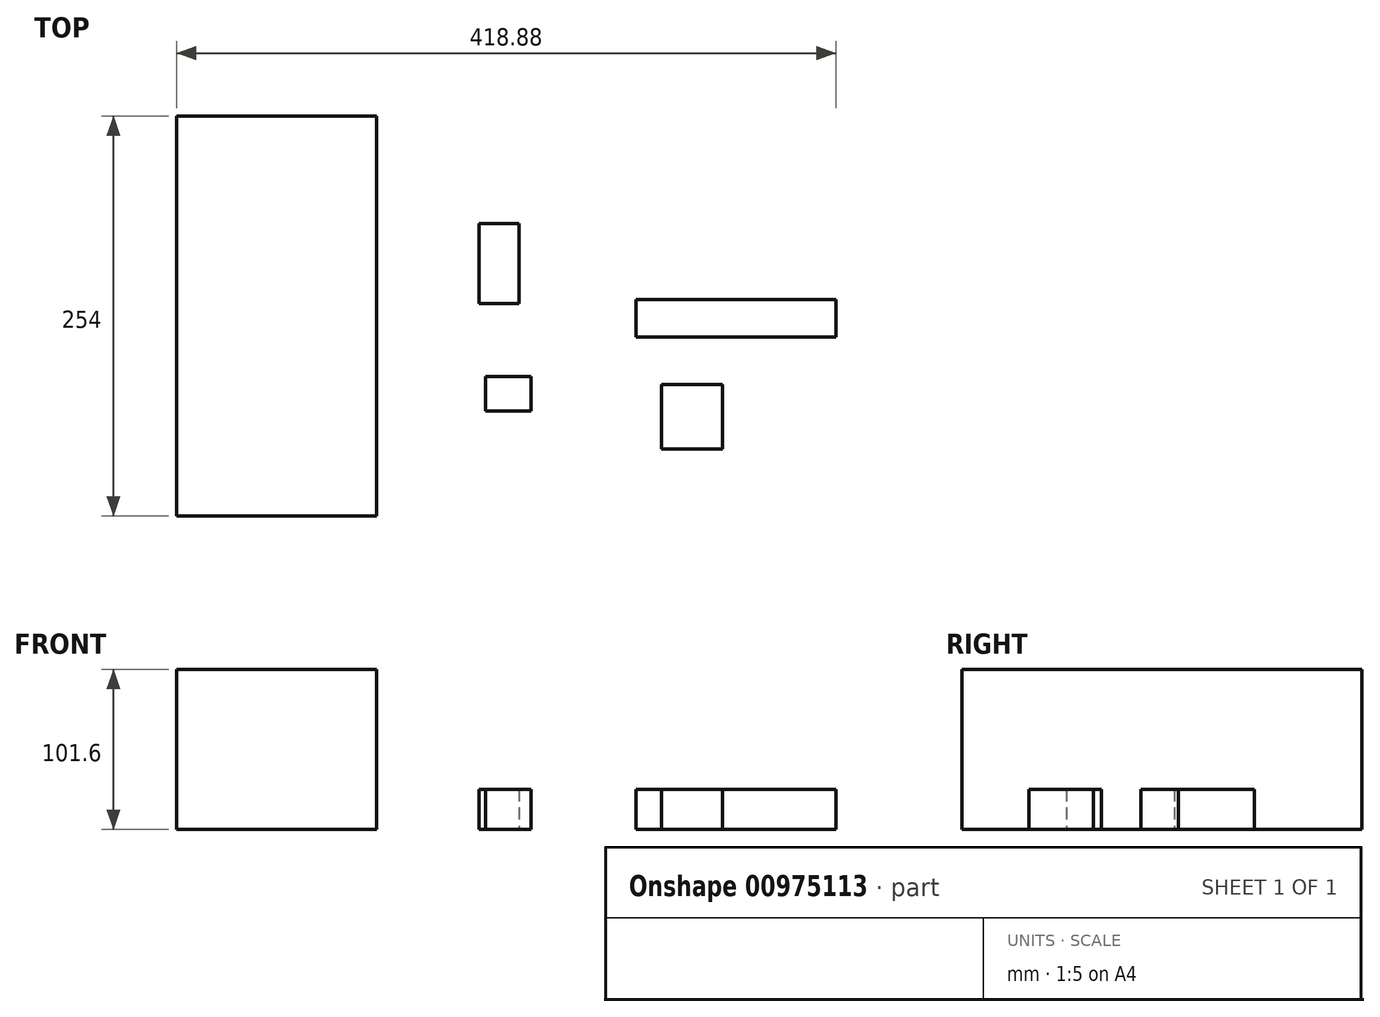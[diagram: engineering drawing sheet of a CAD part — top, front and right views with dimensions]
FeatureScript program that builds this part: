
annotation { "Feature Type Name" : "Feature", "Feature Type Description" : "" }
export const myFeature = defineFeature(function(context is Context, id is Id, definition is map)
    precondition{}
    {
        {
            var Q0;
            Q0=qCreatedBy(makeId("Top.planeOp"),FACE);
            var sketch = newSketch(context, id + "F0", { "sketchPlane" : qUnion([Q0])});
            skLineSegment(sketch, "E0.bottom", {"start": v(-93.4, 74.62) * mm, "end": v(-68, 74.62) * mm});
            skLineSegment(sketch, "E0.top", {"start": v(-93.4, 23.82) * mm, "end": v(-68, 23.82) * mm});
            skLineSegment(sketch, "E0.left", {"start": v(-93.4, 74.62) * mm, "end": v(-93.4, 23.82) * mm});
            skLineSegment(sketch, "E0.right", {"start": v(-68, 74.62) * mm, "end": v(-68, 23.82) * mm});
            skLineSegment(sketch, "E1.bottom", {"start": v(6.4, 26.18) * mm, "end": v(133.4, 26.18) * mm});
            skLineSegment(sketch, "E1.top", {"start": v(6.4, 2.56) * mm, "end": v(133.4, 2.56) * mm});
            skLineSegment(sketch, "E1.left", {"start": v(6.4, 26.18) * mm, "end": v(6.4, 2.56) * mm});
            skLineSegment(sketch, "E1.right", {"start": v(133.4, 26.18) * mm, "end": v(133.4, 2.56) * mm});
            skLineSegment(sketch, "E2.bottom", {"start": v(22.73, -27.56) * mm, "end": v(61.5, -27.56) * mm});
            skLineSegment(sketch, "E2.top", {"start": v(22.73, -68.7) * mm, "end": v(61.5, -68.7) * mm});
            skLineSegment(sketch, "E2.left", {"start": v(22.73, -27.56) * mm, "end": v(22.73, -68.7) * mm});
            skLineSegment(sketch, "E2.right", {"start": v(61.5, -27.56) * mm, "end": v(61.5, -68.7) * mm});
            skLineSegment(sketch, "E3.bottom", {"start": v(-89.06, -22.64) * mm, "end": v(-60.33, -22.64) * mm});
            skLineSegment(sketch, "E3.top", {"start": v(-89.06, -44.68) * mm, "end": v(-60.33, -44.68) * mm});
            skLineSegment(sketch, "E3.left", {"start": v(-89.06, -22.64) * mm, "end": v(-89.06, -44.68) * mm});
            skLineSegment(sketch, "E3.right", {"start": v(-60.33, -22.64) * mm, "end": v(-60.33, -44.68) * mm});
            skSolve(sketch);
        }
        {
            var Q0;
            Q0=makeQuery(id+"F0.imprint","IMPRINT",FACE,{"disambiguationData":[TD([[makeQuery(id+"F0.imprint","IMPRINT",EDGE,{"derivedFrom":sQuery(id+"F0.wireOp",EDGE,"E0.bottom")}),-1.0]])]});
            var Q1;
            Q1=makeQuery(id+"F0.imprint","IMPRINT",FACE,{"disambiguationData":[TD([[makeQuery(id+"F0.imprint","IMPRINT",EDGE,{"derivedFrom":sQuery(id+"F0.wireOp",EDGE,"E1.bottom")}),-1.0]])]});
            var Q2;
            Q2=makeQuery(id+"F0.imprint","IMPRINT",FACE,{"disambiguationData":[TD([[makeQuery(id+"F0.imprint","IMPRINT",EDGE,{"derivedFrom":sQuery(id+"F0.wireOp",EDGE,"E2.bottom")}),-1.0]])]});
            var Q3;
            Q3=makeQuery(id+"F0.imprint","IMPRINT",FACE,{"disambiguationData":[TD([[makeQuery(id+"F0.imprint","IMPRINT",EDGE,{"derivedFrom":sQuery(id+"F0.wireOp",EDGE,"E3.bottom")}),-1.0]])]});
            extrude(context, id + "F1", {"entities" : qUnion([Q0, Q1, Q2, Q3]), "depth" : 25.4 * mm, "offsetDistance" : 25.4 * mm});
        }
        {
            var Q0;
            Q0=qCreatedBy(makeId("Top.planeOp"),FACE);
            var sketch = newSketch(context, id + "F2", { "sketchPlane" : qUnion([Q0])});
            skLineSegment(sketch, "E4.bottom", {"start": v(-285.48, 142.8) * mm, "end": v(-158.48, 142.8) * mm});
            skLineSegment(sketch, "E4.top", {"start": v(-285.48, -111.2) * mm, "end": v(-158.48, -111.2) * mm});
            skLineSegment(sketch, "E4.left", {"start": v(-285.48, 142.8) * mm, "end": v(-285.48, -111.2) * mm});
            skLineSegment(sketch, "E4.right", {"start": v(-158.48, 142.8) * mm, "end": v(-158.48, -111.2) * mm});
            skSolve(sketch);
        }
        {
            var Q0;
            Q0=makeQuery(id+"F2.imprint","IMPRINT",FACE,{"disambiguationData":[TD([[makeQuery(id+"F2.imprint","IMPRINT",EDGE,{"derivedFrom":sQuery(id+"F2.wireOp",EDGE,"E4.bottom")}),-1.0]])]});
            extrude(context, id + "F3", {"entities" : qUnion([Q0]), "depth" : 101.6 * mm, "offsetDistance" : 25.4 * mm});
        }
    });
